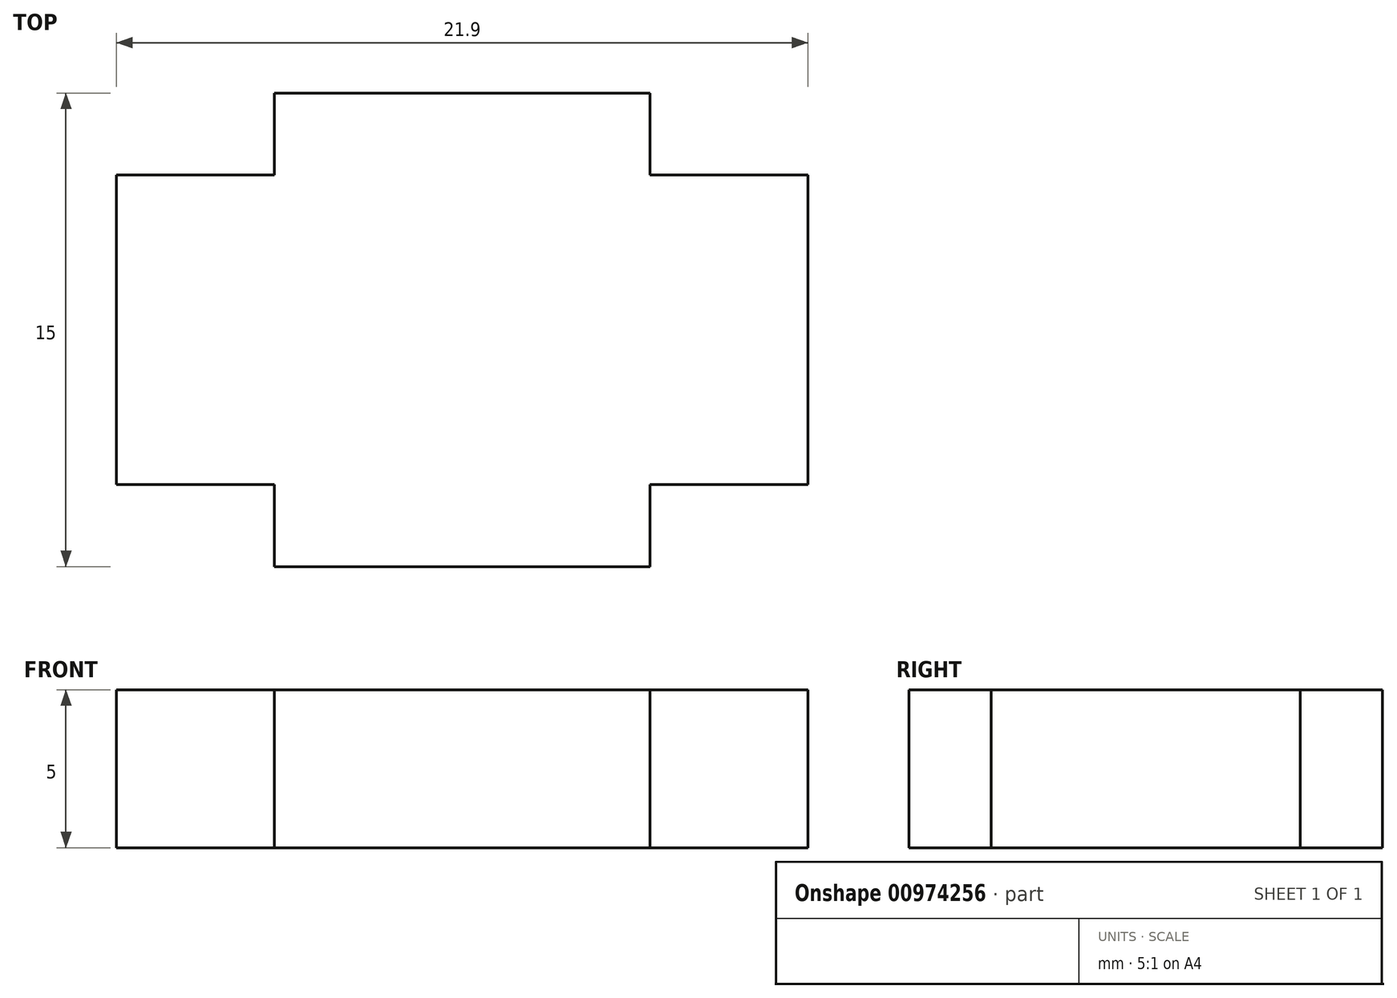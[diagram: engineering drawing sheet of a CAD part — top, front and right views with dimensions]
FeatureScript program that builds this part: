
annotation { "Feature Type Name" : "Feature", "Feature Type Description" : "" }
export const myFeature = defineFeature(function(context is Context, id is Id, definition is map)
    precondition{}
    {
        {
            var Q0;
            Q0=qCreatedBy(makeId("Top.planeOp"),FACE);
            var sketch = newSketch(context, id + "F0", { "sketchPlane" : qUnion([Q0])});
            skLineSegment(sketch, "E0.bottom", {"start": v(5.95, 7.5) * mm, "end": v(-5.95, 7.5) * mm});
            skLineSegment(sketch, "E0.top", {"start": v(5.95, -7.5) * mm, "end": v(-5.95, -7.5) * mm});
            skLineSegment(sketch, "E0.left", {"start": v(5.95, 7.5) * mm, "end": v(5.95, -7.5) * mm});
            skLineSegment(sketch, "E0.right", {"start": v(-5.95, 7.5) * mm, "end": v(-5.95, -7.5) * mm});
            skPoint(sketch, "E0.middle", {"position": v(0, 0) * mm});
            skLineSegment(sketch, "E1", {"start": v(-10.95, 4.9) * mm, "end": v(10.95, 4.9) * mm, "construction": true});
            skLineSegment(sketch, "E2.MirrorCS", {"start": v(-10.95, -4.9) * mm, "end": v(10.95, -4.9) * mm, "construction": true});
            skLineSegment(sketch, "E3", {"start": v(-10.95, 4.9) * mm, "end": v(-10.95, -4.9) * mm, "construction": true});
            skLineSegment(sketch, "E4", {"start": v(-5.95, 4.9) * mm, "end": v(-10.95, 4.9) * mm});
            skLineSegment(sketch, "E5", {"start": v(-10.95, 0) * mm, "end": v(-10.95, 4.9) * mm});
            skLineSegment(sketch, "E6", {"start": v(-10.95, 0) * mm, "end": v(-10.95, -4.9) * mm});
            skLineSegment(sketch, "E7", {"start": v(-10.95, -4.9) * mm, "end": v(-5.95, -4.9) * mm});
            skLineSegment(sketch, "E8", {"start": v(10.95, 4.9) * mm, "end": v(10.95, -4.9) * mm, "construction": true});
            skLineSegment(sketch, "E9", {"start": v(5.95, 4.9) * mm, "end": v(10.95, 4.9) * mm});
            skLineSegment(sketch, "E10", {"start": v(10.95, -4.9) * mm, "end": v(10.95, 4.9) * mm});
            skLineSegment(sketch, "E11", {"start": v(10.95, -4.9) * mm, "end": v(5.95, -4.9) * mm});
            skSolve(sketch);
        }
        {
            var Q0;
            {var subQ0=sQuery(id+"F0.wireOp",EDGE,"E4");Q0=makeQuery(id+"F0.imprint","IMPRINT",FACE,{"disambiguationData":[TD([[makeQuery(id+"F0.imprint","IMPRINT",EDGE,{"derivedFrom":subQ0}),1.0]])]});}
            var Q1;
            {var subQ3=sQuery(id+"F0.wireOp",EDGE,"E0.bottom");Q1=makeQuery(id+"F0.imprint","IMPRINT",FACE,{"disambiguationData":[TD([[makeQuery(id+"F0.imprint","IMPRINT",EDGE,{"derivedFrom":subQ3}),1.0]])]});}
            var Q2;
            {var subQ0=sQuery(id+"F0.wireOp",EDGE,"E9");Q2=makeQuery(id+"F0.imprint","IMPRINT",FACE,{"disambiguationData":[TD([[makeQuery(id+"F0.imprint","IMPRINT",EDGE,{"derivedFrom":subQ0}),-1.0]])]});}
            extrude(context, id + "F1", {"entities" : qUnion([Q0, Q1, Q2]), "depth" : 5 * mm, "offsetDistance" : 25 * mm});
        }
    });
